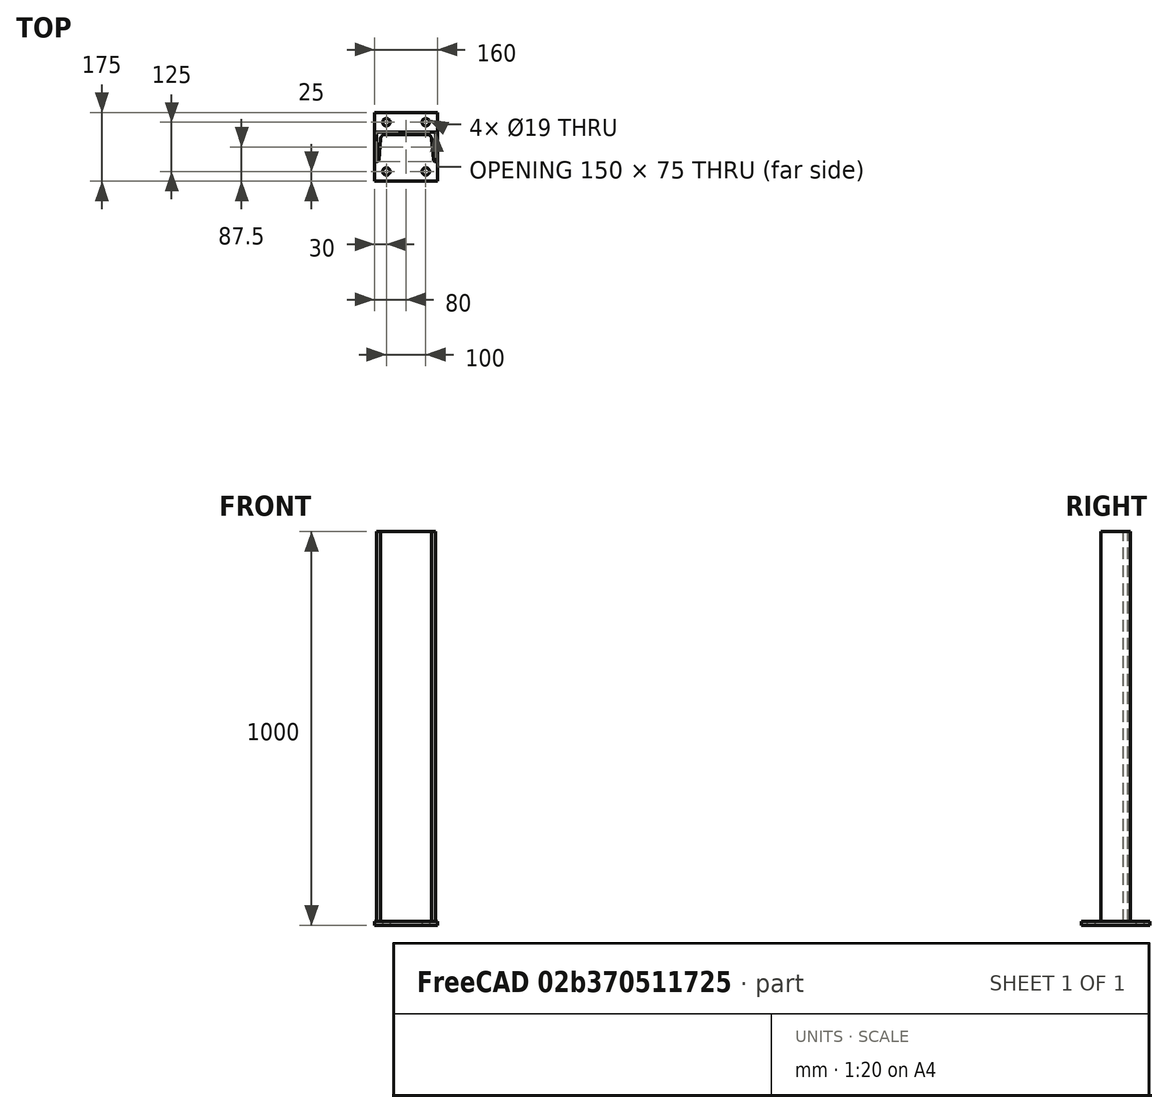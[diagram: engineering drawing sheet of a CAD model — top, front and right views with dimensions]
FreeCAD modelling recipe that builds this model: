
FCSTD DOCUMENT  (FreeCAD 0.21R33668 +26 (Git))
Label: cvPost
License: All rights reserved
LicenseURL: https://en.wikipedia.org/wiki/All_rights_reserved
objects: Part::FeaturePython×2, Part::Extrusion×1, Part::MultiFuse×1, App::Part×1
note: 4 computed .brp shape members not serialized (recipe doc carries the construction recipe); baked Part::Feature solids carry a one-line shape summary decoded from their .brp

FEATURE [Part::FeaturePython] BasePlate  # WARN: FeaturePython — macro-defined, semantics opaque (R4)
  B = 175
  D = 19
  H = 160
  b1 = 25
  h1 = 30
  sface = 0
FEATURE [Part::Extrusion] Extrude
  Base = -> BasePlate
  Dir = (0,0,1)
  DirMode = 2
  FaceMakerClass = Part::FaceMakerBullseye
  LengthFwd = 10
  LengthRev = 0
  Solid = true
  Symmetric = false
FEATURE [Part::FeaturePython] Channel  # WARN: FeaturePython — macro-defined, semantics opaque (R4)
  B = 75
  H = 150
  L = 1000
  Solid = true
  g0 = 7.85
  mass = 16.9049
  size = 3
  standard = SS
FEATURE [Part::MultiFuse] Fusion  label="PostC"
  Placement = pos=(0,-37.5,-1000) rot=(0,0,1;4.71239rad)
  Shapes = -> [Extrude,Channel]
FEATURE [App::Part] Part  label="post"
  Group = -> [BasePlate,Channel,Extrude,Fusion]
  Origin = -> Origin
